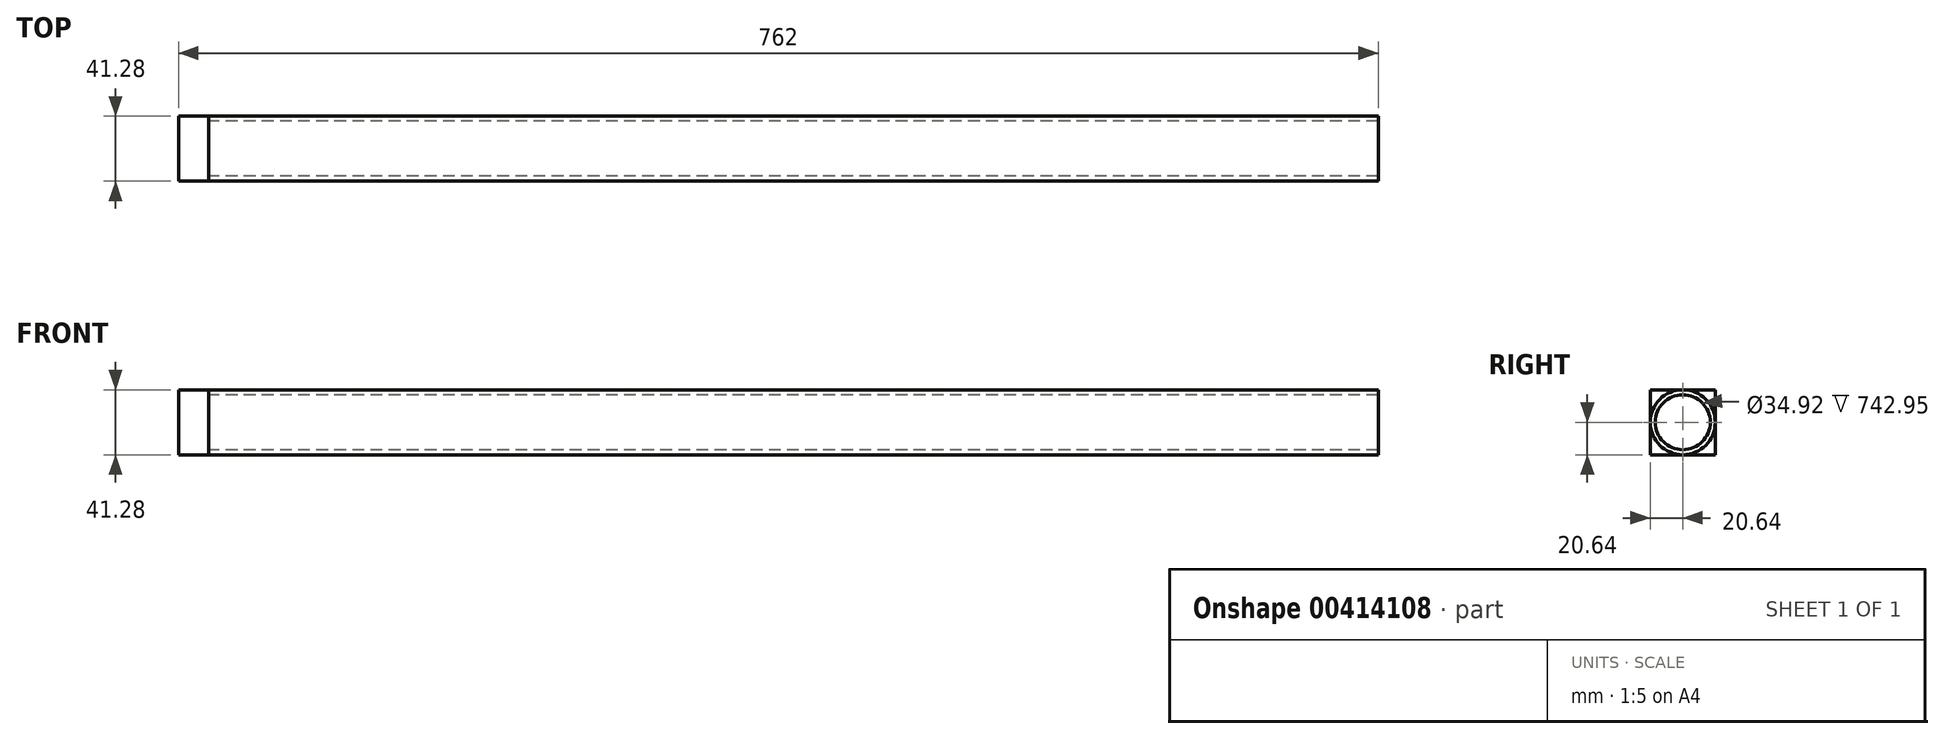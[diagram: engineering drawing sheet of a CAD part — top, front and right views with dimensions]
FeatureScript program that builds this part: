
annotation { "Feature Type Name" : "Feature", "Feature Type Description" : "" }
export const myFeature = defineFeature(function(context is Context, id is Id, definition is map)
    precondition{}
    {
        {
            var Q0;
            Q0=qCreatedBy(makeId("Right.planeOp"),FACE);
            var sketch = newSketch(context, id + "F0", { "sketchPlane" : qUnion([Q0])});
            skCircle(sketch, "E0", {"center": v(0, 0) * mm, "radius": 20.64 * mm});
            skCircle(sketch, "E1", {"center": v(0, 0) * mm, "radius": 17.46 * mm});
            skSolve(sketch);
        }
        {
            var Q0;
            Q0 = qSketchRegion(id + "F0", true);
            extrude(context, id + "F1", {"entities" : qUnion([Q0]), "endBound" : BoundingType.SYMMETRIC, "depth" : 762 * mm});
        }
        {
            var Q0;
            Q0=makeQuery(id+"F1.opExtrude","CAP_FACE",FACE,{"disambiguationData":[OSD([sQuery(id+"F0.wireOp",EDGE,"E0"),sQuery(id+"F0.wireOp",EDGE,"E1")])],"isStart":true});
            var sketch = newSketch(context, id + "F2", { "sketchPlane" : qUnion([Q0])});
            skLineSegment(sketch, "E2.bottom", {"start": v(20.64, 20.64) * mm, "end": v(-20.64, 20.64) * mm});
            skLineSegment(sketch, "E2.top", {"start": v(20.64, -20.64) * mm, "end": v(-20.64, -20.64) * mm});
            skLineSegment(sketch, "E2.left", {"start": v(20.64, 20.64) * mm, "end": v(20.64, -20.64) * mm});
            skLineSegment(sketch, "E2.right", {"start": v(-20.64, 20.64) * mm, "end": v(-20.64, -20.64) * mm});
            skPoint(sketch, "E2.middle", {"position": v(0, 0) * mm});
            skSolve(sketch);
        }
        {
            var Q0;
            Q0 = qSketchRegion(id + "F2", true);
            extrude(context, id + "F3", {"entities" : qUnion([Q0]), "operationType" : NewBodyOperationType.ADD, "oppositeDirection" : true, "depth" : 19.05 * mm});
        }
    });
